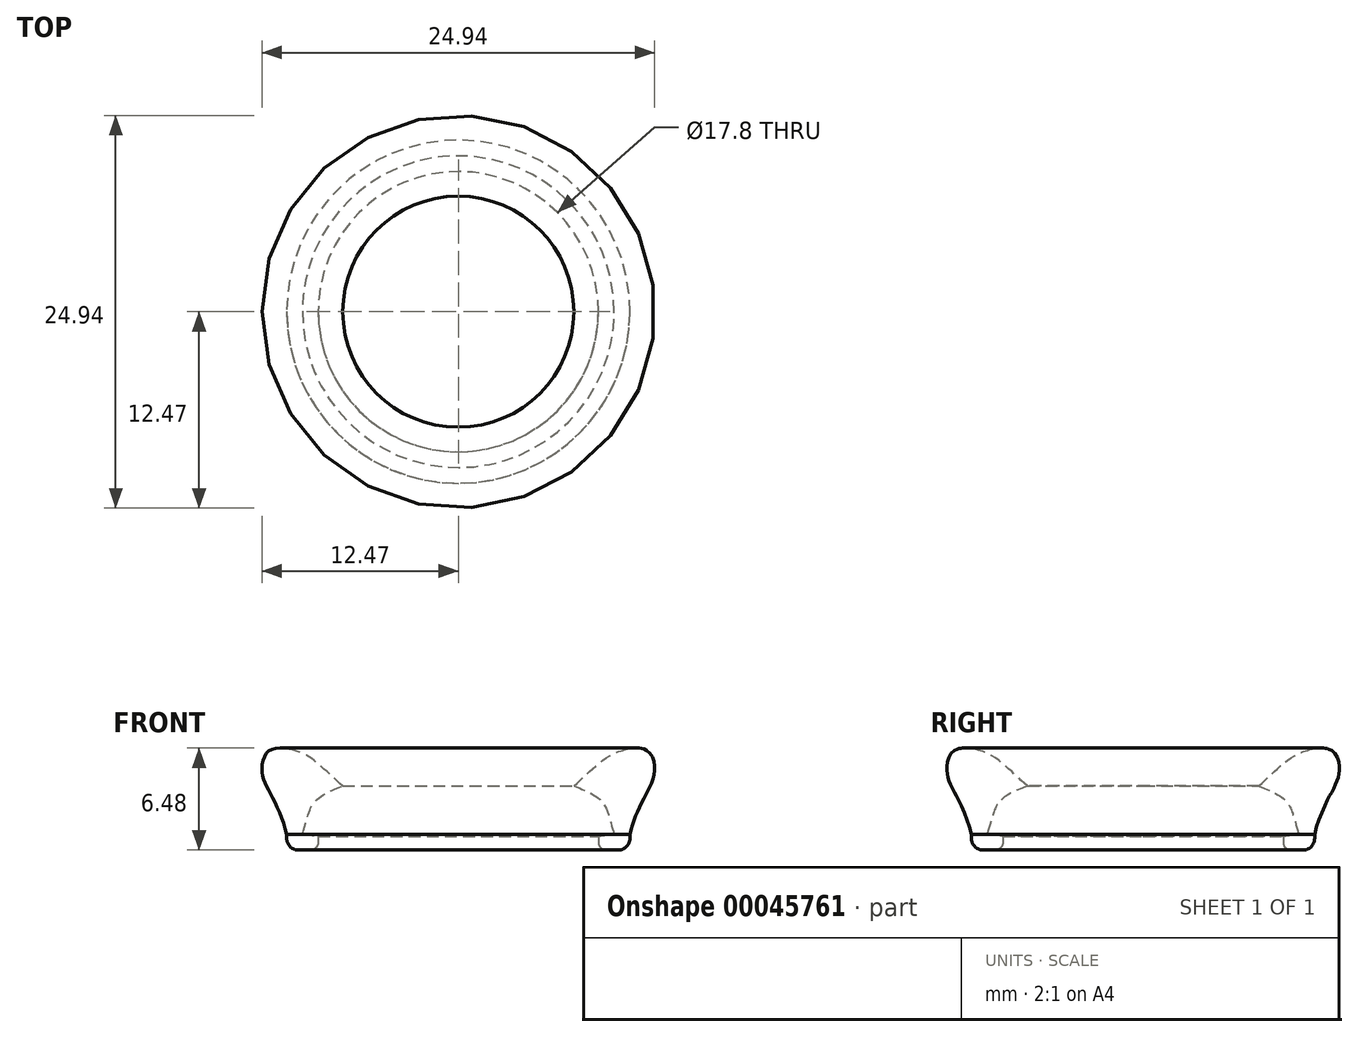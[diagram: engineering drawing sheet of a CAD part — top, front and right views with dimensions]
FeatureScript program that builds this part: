
annotation { "Feature Type Name" : "Feature", "Feature Type Description" : "" }
export const myFeature = defineFeature(function(context is Context, id is Id, definition is map)
    precondition{}
    {
        {
            var Q0;
            Q0=qCreatedBy(makeId("Front.planeOp"),FACE);
            var sketch = newSketch(context, id + "F0", { "sketchPlane" : qUnion([Q0])});
            skLineSegment(sketch, "E0", {"start": v(0, 0) * mm, "end": v(0, 6.5) * mm, "construction": true});
            skLineSegment(sketch, "E1", {"start": v(0, 0) * mm, "end": v(-5, 0) * mm});
            skLineSegment(sketch, "E2", {"start": v(-5, 0) * mm, "end": v(-5, 2) * mm, "construction": true});
            skLineSegment(sketch, "E3", {"start": v(-9.9, 2) * mm, "end": v(0, 2) * mm, "construction": true});
            skFitSpline(sketch, "E4", {"points": [v(-9.9, 2) * mm, v(-5, 0) * mm], "startDerivative": vector(5.68, 0) * mm, "endDerivative": vector(2.04, -1.3) * mm});
            skLineSegment(sketch, "E5", {"start": v(-8.6, 4.5) * mm, "end": v(-8.6, 2) * mm, "construction": true});
            skLineSegment(sketch, "E6", {"start": v(-8.6, 4.5) * mm, "end": v(0, 4.5) * mm, "construction": true});
            skFitSpline(sketch, "E7", {"points": [v(-9.9, 2) * mm, v(-8.6, 4.5) * mm, v(0, 6.5) * mm], "startDerivative": vector(3.8, 12.24) * mm, "endDerivative": vector(12.87, 0.22) * mm});
            skLineSegment(sketch, "E8", {"start": v(-9.9, 2) * mm, "end": v(-10.9, 2) * mm, "construction": true});
            skLineSegment(sketch, "E9", {"start": v(-10.9, 2) * mm, "end": v(-10.9, 1) * mm});
            skLineSegment(sketch, "E10", {"start": v(-10.9, 1) * mm, "end": v(-8.9, 1) * mm});
            skLineSegment(sketch, "E11", {"start": v(-8.9, 1) * mm, "end": v(-8.9, 1.88) * mm});
            skFitSpline(sketch, "E12", {"points": [v(-7.34, 5.08) * mm, v(-9.01, 6.58) * mm, v(-10.41, 7.33) * mm, v(-12.02, 7.3) * mm, v(-12.46, 6.03) * mm, v(-11.98, 4.68) * mm, v(-10.9, 2) * mm], "startDerivative": vector(-8.56, 7.12) * mm, "endDerivative": vector(3.12, -14.59) * mm});
            skSolve(sketch);
        }
        {
            var Q0;
            Q0=qSketchRegion(id+"F0",true);
            var Q1;
            Q1=sQuery(id+"F0.wireOp",EDGE,"E0");
            revolve(context, id + "F1", {"entities" : qUnion([Q0]), "axis" : qUnion([Q1]), "revolveType" : RevolveType.FULL});
        }
        {
            var Q0;
            Q0=makeQuery(id+"F1.opRevolve","SWEPT_FACE",FACE,{"disambiguationData":[OSD([sQuery(id+"F0.wireOp",EDGE,"E10")])]});
            var sketch = newSketch(context, id + "F2", { "sketchPlane" : qUnion([Q0])});
            skLineSegment(sketch, "E13", {"start": v(0, 0) * mm, "end": v(0, 12.47) * mm, "construction": true});
            skLineSegment(sketch, "E14", {"start": v(-3.5, 12.47) * mm, "end": v(3.5, 12.47) * mm});
            skLineSegment(sketch, "E15", {"start": v(-3.5, 12.47) * mm, "end": v(-3.5, 0) * mm});
            skLineSegment(sketch, "E16", {"start": v(3.5, 12.47) * mm, "end": v(3.5, 0) * mm});
            skLineSegment(sketch, "E17.1.0", {"start": v(0, 0) * mm, "end": v(-10.8, -6.23) * mm, "construction": true});
            skLineSegment(sketch, "E17.1.1", {"start": v(-9.05, -9.26) * mm, "end": v(-12.55, -3.2) * mm});
            skLineSegment(sketch, "E17.1.2", {"start": v(-9.05, -9.26) * mm, "end": v(1.75, -3.03) * mm});
            skLineSegment(sketch, "E17.1.3", {"start": v(-12.55, -3.2) * mm, "end": v(-1.75, 3.03) * mm});
            skLineSegment(sketch, "E17.2.0", {"start": v(0, 0) * mm, "end": v(10.8, -6.23) * mm, "construction": true});
            skLineSegment(sketch, "E17.2.1", {"start": v(12.55, -3.2) * mm, "end": v(9.05, -9.26) * mm});
            skLineSegment(sketch, "E17.2.2", {"start": v(12.55, -3.2) * mm, "end": v(1.75, 3.03) * mm});
            skLineSegment(sketch, "E17.2.3", {"start": v(9.05, -9.26) * mm, "end": v(-1.75, -3.03) * mm});
            skPoint(sketch, "E17.center", {"position": v(0, 0) * mm});
            skCircle(sketch, "E18", {"center": v(0, 0) * mm, "radius": 12.47 * mm, "construction": true});
            skSolve(sketch);
        }
        {
            var Q0;
            {var subQ0=sQuery(id+"F0.wireOp",EDGE,"E10");var subQ1=sQuery(id+"F0.wireOp",EDGE,"E11");Q0=makeQuery(id+"FoXXn5hXKdBAvWS_1.boolean.opBoolean","SPLIT",EDGE,{"disambiguationData":[TD([makeQuery(id+"FoXXn5hXKdBAvWS_1.opExtrude","SWEPT_FACE",FACE,{"disambiguationData":[OSD([sQuery(id+"F2.wireOp",EDGE,"E15")])]})])],"derivedFrom":makeQuery(id+"F1.opRevolve","SWEPT_EDGE",EDGE,{"disambiguationData":[OSD([subQ0,subQ1])]})});}
            var Q1;
            {var subQ0=sQuery(id+"F0.wireOp",EDGE,"E10");var subQ1=sQuery(id+"F0.wireOp",EDGE,"E11");Q1=makeQuery(id+"FoXXn5hXKdBAvWS_1.boolean.opBoolean","SPLIT",EDGE,{"disambiguationData":[TD([makeQuery(id+"FoXXn5hXKdBAvWS_1.opExtrude","SWEPT_FACE",FACE,{"disambiguationData":[OSD([sQuery(id+"F2.wireOp",EDGE,"E17.1.2")])]})])],"derivedFrom":makeQuery(id+"F1.opRevolve","SWEPT_EDGE",EDGE,{"disambiguationData":[OSD([subQ0,subQ1])]})});}
            var Q2;
            {var subQ0=sQuery(id+"F0.wireOp",EDGE,"E10");var subQ1=sQuery(id+"F0.wireOp",EDGE,"E11");Q2=makeQuery(id+"FoXXn5hXKdBAvWS_1.boolean.opBoolean","SPLIT",EDGE,{"disambiguationData":[TD([makeQuery(id+"FoXXn5hXKdBAvWS_1.opExtrude","SWEPT_FACE",FACE,{"disambiguationData":[OSD([sQuery(id+"F2.wireOp",EDGE,"E16")])]})])],"derivedFrom":makeQuery(id+"F1.opRevolve","SWEPT_EDGE",EDGE,{"disambiguationData":[OSD([subQ0,subQ1])]})});}
            fillet(context, id + "F3", {"entities" : qUnion([Q0, Q1, Q2]), "radius" : 0.5 * mm, "allowEdgeOverflow" : false});
        }
        {
            var Q0;
            {var subQ0=sQuery(id+"F0.wireOp",EDGE,"E9");var subQ1=sQuery(id+"F0.wireOp",EDGE,"E10");Q0=makeQuery(id+"FoXXn5hXKdBAvWS_1.boolean.opBoolean","SPLIT",EDGE,{"disambiguationData":[TD([makeQuery(id+"FoXXn5hXKdBAvWS_1.opExtrude","SWEPT_FACE",FACE,{"disambiguationData":[OSD([sQuery(id+"F2.wireOp",EDGE,"E15")])]})])],"derivedFrom":makeQuery(id+"F1.opRevolve","SWEPT_EDGE",EDGE,{"disambiguationData":[OSD([subQ0,subQ1])]})});}
            var Q1;
            {var subQ0=sQuery(id+"F0.wireOp",EDGE,"E9");var subQ1=sQuery(id+"F0.wireOp",EDGE,"E10");Q1=makeQuery(id+"FoXXn5hXKdBAvWS_1.boolean.opBoolean","SPLIT",EDGE,{"disambiguationData":[TD([makeQuery(id+"FoXXn5hXKdBAvWS_1.opExtrude","SWEPT_FACE",FACE,{"disambiguationData":[OSD([sQuery(id+"F2.wireOp",EDGE,"E16")])]})])],"derivedFrom":makeQuery(id+"F1.opRevolve","SWEPT_EDGE",EDGE,{"disambiguationData":[OSD([subQ0,subQ1])]})});}
            var Q2;
            {var subQ0=sQuery(id+"F0.wireOp",EDGE,"E9");var subQ1=sQuery(id+"F0.wireOp",EDGE,"E10");Q2=makeQuery(id+"FoXXn5hXKdBAvWS_1.boolean.opBoolean","SPLIT",EDGE,{"disambiguationData":[TD([makeQuery(id+"FoXXn5hXKdBAvWS_1.opExtrude","SWEPT_FACE",FACE,{"disambiguationData":[OSD([sQuery(id+"F2.wireOp",EDGE,"E17.1.2")])]})])],"derivedFrom":makeQuery(id+"F1.opRevolve","SWEPT_EDGE",EDGE,{"disambiguationData":[OSD([subQ0,subQ1])]})});}
            fillet(context, id + "F4", {"entities" : qUnion([Q0, Q1, Q2]), "radius" : 0.75 * mm, "allowEdgeOverflow" : false});
        }
    });
